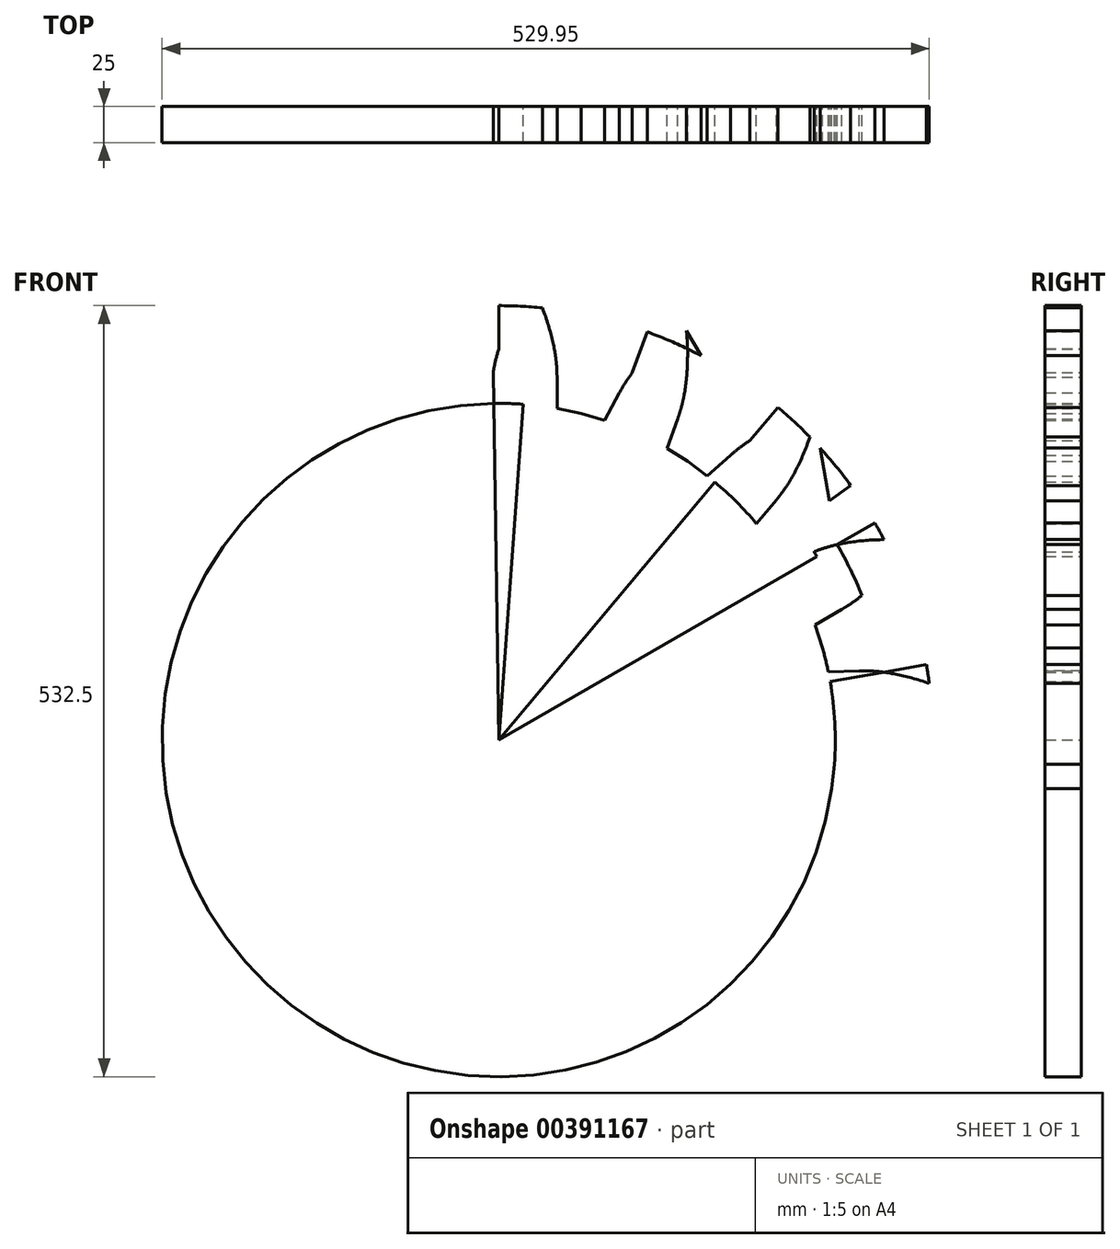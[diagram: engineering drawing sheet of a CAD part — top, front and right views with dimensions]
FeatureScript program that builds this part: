
annotation { "Feature Type Name" : "Feature", "Feature Type Description" : "" }
export const myFeature = defineFeature(function(context is Context, id is Id, definition is map)
    precondition{}
    {
        {
            var Q0;
            Q0=qCreatedBy(makeId("Front.planeOp"),FACE);
            var sketch = newSketch(context, id + "F0", { "sketchPlane" : qUnion([Q0])});
            skCircle(sketch, "E0", {"center": v(0, 0) * mm, "radius": 232.5 * mm});
            skCircle(sketch, "E1", {"center": v(0, 0) * mm, "radius": 253.72 * mm});
            skCircle(sketch, "E2", {"center": v(0, 0) * mm, "radius": 270 * mm});
            skCircle(sketch, "E3", {"center": v(0, 0) * mm, "radius": 300 * mm});
            skLineSegment(sketch, "E4", {"start": v(0, 0) * mm, "end": v(0, 396.68) * mm});
            skLineSegment(sketch, "E5", {"start": v(0, 0) * mm, "end": v(136.8, 375.88) * mm});
            skLineSegment(sketch, "E6", {"start": v(0, 0) * mm, "end": v(257.12, 306.42) * mm});
            skLineSegment(sketch, "E7", {"start": v(0, 0) * mm, "end": v(346.41, 200) * mm});
            skLineSegment(sketch, "E8", {"start": v(0, 270) * mm, "end": v(86.78, 238.41) * mm});
            skLineSegment(sketch, "E9", {"start": v(163.08, 194.36) * mm, "end": v(21.6, 313.07) * mm});
            skLineSegment(sketch, "E10", {"start": v(219.72, 126.86) * mm, "end": v(81.2, 366.78) * mm});
            skLineSegment(sketch, "E11", {"start": v(0, 0) * mm, "end": v(393.92, 69.46) * mm});
            skLineSegment(sketch, "E12", {"start": v(249.86, 44.06) * mm, "end": v(185.72, 407.83) * mm});
            skLineSegment(sketch, "E13", {"start": v(-5.96, 399.96) * mm, "end": v(0, 0) * mm});
            skFitSpline(sketch, "E14", {"points": [v(-3.78, 253.69) * mm, v(0, 270) * mm, v(21.6, 313.07) * mm, v(81.2, 366.78) * mm, v(185.72, 407.83) * mm], "startDerivative": vector(18.73, 108.77) * mm, "endDerivative": vector(322.57, 102.04) * mm});
            skLineSegment(sketch, "E15", {"start": v(21.69, 299.21) * mm, "end": v(0, 0) * mm});
            skFitSpline(sketch, "E16.MirrorCS", {"points": [v(40.33, 250.49) * mm, v(38.94, 267.18) * mm, v(23.77, 312.92) * mm, v(-27.46, 374.65) * mm, v(-124.96, 430.35) * mm], "startDerivative": vector(-2.85, 110.33) * mm, "endDerivative": vector(-304.48, 147.49) * mm});
            skFitSpline(sketch, "E17", {"points": [v(40.33, 250.49) * mm, v(40.33, 228.98) * mm], "startDerivative": vector(0, -16.2) * mm, "endDerivative": vector(0, -16.2) * mm});
            skFitSpline(sketch, "E18", {"points": [v(40.33, 228.98) * mm, v(56.82, 225.45) * mm], "startDerivative": vector(16.5, -3.53) * mm, "endDerivative": vector(16.5, -3.53) * mm});
            skArc(sketch, "E19.filletArc", {"start": v(40.33, 241.1) * mm, "mid": v(43.67, 231.67) * mm, "end": v(52.2, 226.44) * mm});
            skArc(sketch, "E20.MirrorCS", {"start": v(78.77, 231.42) * mm, "mid": v(71.36, 224.7) * mm, "end": v(61.37, 224.13) * mm});
            skFitSpline(sketch, "E21.MirrorCS", {"points": [v(73.02, 220.74) * mm, v(56.82, 225.45) * mm], "startDerivative": vector(-16.2, 4.71) * mm, "endDerivative": vector(-16.2, 4.71) * mm});
            skFitSpline(sketch, "E22.MirrorCS", {"points": [v(83.21, 239.68) * mm, v(92.35, 253.72) * mm, v(127.38, 286.8) * mm, v(201.75, 316.88) * mm, v(314, 319.71) * mm], "startDerivative": vector(54.8, 95.8) * mm, "endDerivative": vector(338.01, -14.44) * mm});
            skFitSpline(sketch, "E23.MirrorCS", {"points": [v(123.57, 221.59) * mm, v(127.97, 237.75) * mm, v(129.36, 285.91) * mm, v(102.33, 361.45) * mm, v(29.76, 447.13) * mm], "startDerivative": vector(35.06, 104.65) * mm, "endDerivative": vector(-235.67, 242.73) * mm});
            skFitSpline(sketch, "E24.MirrorCS", {"points": [v(83.21, 239.68) * mm, v(73.02, 220.74) * mm], "startDerivative": vector(-7.68, -14.27) * mm, "endDerivative": vector(-7.68, -14.27) * mm});
            skArc(sketch, "E25.MirrorCS", {"start": v(120.36, 212.77) * mm, "mid": v(120.27, 202.77) * mm, "end": v(126.5, 194.93) * mm});
            skFitSpline(sketch, "E26.MirrorCS", {"points": [v(116.21, 201.37) * mm, v(130.5, 192.42) * mm], "startDerivative": vector(14.3, -8.95) * mm, "endDerivative": vector(14.3, -8.95) * mm});
            skArc(sketch, "E27.MirrorCS", {"start": v(153.17, 190.52) * mm, "mid": v(143.9, 186.74) * mm, "end": v(134.32, 189.62) * mm});
            skFitSpline(sketch, "E28.MirrorCS", {"points": [v(144.1, 182.45) * mm, v(130.5, 192.42) * mm], "startDerivative": vector(-13.6, 9.97) * mm, "endDerivative": vector(-13.6, 9.97) * mm});
            skFitSpline(sketch, "E29.MirrorCS", {"points": [v(160.17, 196.77) * mm, v(173.55, 206.83) * mm, v(217.79, 225.94) * mm, v(297.97, 228.77) * mm, v(404.41, 193.03) * mm], "startDerivative": vector(84.26, 71.28) * mm, "endDerivative": vector(312.69, -129.18) * mm});
            skFitSpline(sketch, "E30.MirrorCS", {"points": [v(191.9, 165.96) * mm, v(201.57, 179.64) * mm, v(219.35, 224.43) * mm, v(219.79, 304.65) * mm, v(180.9, 409.99) * mm], "startDerivative": vector(68.74, 86.35) * mm, "endDerivative": vector(-138.44, 308.7) * mm});
            skArc(sketch, "E31.MirrorCS", {"start": v(185.87, 158.78) * mm, "mid": v(182.37, 149.4) * mm, "end": v(185.53, 139.91) * mm});
            skFitSpline(sketch, "E32.MirrorCS", {"points": [v(191.9, 165.96) * mm, v(178.08, 149.48) * mm], "startDerivative": vector(-10.41, -12.41) * mm, "endDerivative": vector(-10.41, -12.41) * mm});
            skFitSpline(sketch, "E33.MirrorCS", {"points": [v(217.8, 130.12) * mm, v(197.82, 122.16) * mm], "startDerivative": vector(-15.05, -6) * mm, "endDerivative": vector(-15.05, -6) * mm});
            skArc(sketch, "E34.MirrorCS", {"start": v(209.1, 126.65) * mm, "mid": v(199.1, 126.26) * mm, "end": v(191.08, 132.25) * mm});
            skFitSpline(sketch, "E35.MirrorCS", {"points": [v(217.8, 130.12) * mm, v(233.83, 135) * mm, v(281.93, 137.83) * mm, v(358.24, 113.06) * mm, v(446.05, 43.08) * mm], "startDerivative": vector(103.56, 38.16) * mm, "endDerivative": vector(249.65, -228.33) * mm});
            skFitSpline(sketch, "E36.MirrorCS", {"points": [v(237.1, 90.32) * mm, v(250.85, 99.87) * mm, v(282.88, 135.87) * mm, v(310.73, 211.1) * mm, v(310.2, 323.4) * mm], "startDerivative": vector(94.12, 57.63) * mm, "endDerivative": vector(-24.51, 337.43) * mm});
            skFitSpline(sketch, "E37.MirrorCS", {"points": [v(123.57, 221.59) * mm, v(116.21, 201.37) * mm], "startDerivative": vector(-5.54, -15.22) * mm, "endDerivative": vector(-5.54, -15.22) * mm});
            skFitSpline(sketch, "E38.MirrorCS", {"points": [v(160.17, 196.77) * mm, v(144.1, 182.45) * mm], "startDerivative": vector(-12.1, -10.78) * mm, "endDerivative": vector(-12.1, -10.78) * mm});
            skLineSegment(sketch, "E39", {"start": v(0, 0) * mm, "end": v(327.9, 236.96) * mm});
            skFitSpline(sketch, "E40.MirrorCS", {"points": [v(217.8, 130.12) * mm, v(197.82, 122.16) * mm], "startDerivative": vector(-15.05, -6) * mm, "endDerivative": vector(-15.05, -6) * mm});
            skArc(sketch, "E41.MirrorCS", {"start": v(228.97, 85.63) * mm, "mid": v(222.47, 78.02) * mm, "end": v(222.2, 68.02) * mm});
            skFitSpline(sketch, "E42.MirrorCS", {"points": [v(237.1, 90.32) * mm, v(218.46, 79.56) * mm], "startDerivative": vector(-14.03, -8.1) * mm, "endDerivative": vector(-14.03, -8.1) * mm});
            skFitSpline(sketch, "E43.MirrorCS", {"points": [v(218.46, 79.56) * mm, v(223.66, 63.52) * mm], "startDerivative": vector(5.2, -16.05) * mm, "endDerivative": vector(5.2, -16.05) * mm});
            skArc(sketch, "E44.MirrorCS", {"start": v(239.8, 47.5) * mm, "mid": v(230.27, 50.55) * mm, "end": v(224.78, 58.92) * mm});
            skFitSpline(sketch, "E45.MirrorCS", {"points": [v(249.18, 47.78) * mm, v(227.67, 47.14) * mm], "startDerivative": vector(-16.2, -0.48) * mm, "endDerivative": vector(-16.2, -0.48) * mm});
            skFitSpline(sketch, "E46.MirrorCS", {"points": [v(249.18, 47.78) * mm, v(265.9, 46.89) * mm, v(312.07, 33.09) * mm, v(375.3, -16.28) * mm, v(433.88, -112.08) * mm], "startDerivative": vector(110.36, 0.44) * mm, "endDerivative": vector(156.5, -299.95) * mm});
            skFitSpline(sketch, "E47.MirrorCS", {"points": [v(253.69, 3.78) * mm, v(269.88, 8.05) * mm, v(312.3, 30.93) * mm, v(364.2, 92.1) * mm, v(402.1, 197.8) * mm], "startDerivative": vector(108.16, 21.96) * mm, "endDerivative": vector(92.38, 325.46) * mm});
            skFitSpline(sketch, "E48.MirrorCS", {"points": [v(217.8, 130.12) * mm, v(233.83, 135) * mm, v(281.93, 137.83) * mm, v(358.24, 113.06) * mm, v(446.05, 43.08) * mm], "startDerivative": vector(103.56, 38.16) * mm, "endDerivative": vector(249.65, -228.33) * mm});
            skFitSpline(sketch, "E49.MirrorCS", {"points": [v(237.1, 90.32) * mm, v(250.85, 99.87) * mm, v(282.88, 135.87) * mm, v(310.73, 211.1) * mm, v(310.2, 323.4) * mm], "startDerivative": vector(94.12, 57.63) * mm, "endDerivative": vector(-24.51, 337.43) * mm});
            skFitSpline(sketch, "E50.MirrorCS", {"points": [v(250.49, -40.33) * mm, v(265.9, -46.89) * mm, v(304.57, -75.64) * mm, v(347.1, -143.66) * mm, v(369.38, -253.71) * mm], "startDerivative": vector(103.86, -37.33) * mm, "endDerivative": vector(44.47, -335.38) * mm});
            skFitSpline(sketch, "E51.MirrorCS", {"points": [v(239.68, -83.21) * mm, v(256.36, -84.74) * mm, v(304.03, -77.75) * mm, v(373.73, -38.01) * mm, v(445.5, 48.33) * mm], "startDerivative": vector(109.15, -16.36) * mm, "endDerivative": vector(198.12, 274.24) * mm});
            skArc(sketch, "E52.MirrorCS", {"start": v(241.58, -37.38) * mm, "mid": v(233.67, -31.25) * mm, "end": v(231.38, -21.52) * mm});
            skFitSpline(sketch, "E53.MirrorCS", {"points": [v(250.49, -40.33) * mm, v(230.06, -33.58) * mm], "startDerivative": vector(-15.38, 5.08) * mm, "endDerivative": vector(-15.38, 5.08) * mm});
            skFitSpline(sketch, "E54.MirrorCS", {"points": [v(230.06, -33.58) * mm, v(231.9, -16.8) * mm], "startDerivative": vector(1.83, 16.77) * mm, "endDerivative": vector(1.83, 16.77) * mm});
            skSolve(sketch);
        }
        {
            var Q0;
            {var subQ5=sQuery(id+"F0.wireOp",EDGE,"E54.MirrorCS");Q0=makeQuery(id+"F0.imprint","IMPRINT",FACE,{"disambiguationData":[TD([[makeQuery(id+"F0.imprint","IMPRINT",EDGE,{"derivedFrom":subQ5}),1.0]])]});}
            var Q1;
            {var subQ1=sQuery(id+"F0.wireOp",EDGE,"E4");var subQ3=sQuery(id+"F0.wireOp",EDGE,"E0");var subQ4=makeQuery(id+"F0.imprint","INTERSECT",VERTEX,{"derivedFrom":[subQ1,subQ3]});Q1=makeQuery(id+"F0.imprint","IMPRINT",FACE,{"disambiguationData":[TD([[makeQuery(id+"F0.imprint","IMPRINT",EDGE,{"disambiguationData":[TD([[subQ4,-1.0]])],"derivedFrom":subQ3}),-1.0]])]});}
            var Q2;
            {var subQ1=sQuery(id+"F0.wireOp",EDGE,"E4");var subQ3=sQuery(id+"F0.wireOp",EDGE,"E0");var subQ4=makeQuery(id+"F0.imprint","INTERSECT",VERTEX,{"derivedFrom":[subQ1,subQ3]});Q2=makeQuery(id+"F0.imprint","IMPRINT",FACE,{"disambiguationData":[TD([[makeQuery(id+"F0.imprint","IMPRINT",EDGE,{"disambiguationData":[TD([[subQ4,1.0]])],"derivedFrom":subQ3}),-1.0]])]});}
            var Q3;
            {var subQ0=sQuery(id+"F0.wireOp",EDGE,"E17");Q3=makeQuery(id+"F0.imprint","IMPRINT",FACE,{"disambiguationData":[TD([[makeQuery(id+"F0.imprint","IMPRINT",EDGE,{"derivedFrom":subQ0}),-1.0]])]});}
            var Q4;
            {var subQ0=sQuery(id+"F0.wireOp",EDGE,"E15");var subQ1=sQuery(id+"F0.wireOp",EDGE,"E1");var subQ2=makeQuery(id+"F0.imprint","INTERSECT",VERTEX,{"derivedFrom":[subQ1,subQ0]});Q4=makeQuery(id+"F0.imprint","IMPRINT",FACE,{"disambiguationData":[TD([[makeQuery(id+"F0.imprint","IMPRINT",EDGE,{"disambiguationData":[TD([[subQ2,-1.0]])],"derivedFrom":subQ1}),1.0]])]});}
            var Q5;
            {var subQ0=sQuery(id+"F0.wireOp",EDGE,"E16.MirrorCS");var subQ1=sQuery(id+"F0.wireOp",EDGE,"E2");var subQ2=makeQuery(id+"F0.imprint","INTERSECT",VERTEX,{"derivedFrom":[subQ1,subQ0]});Q5=makeQuery(id+"F0.imprint","IMPRINT",FACE,{"disambiguationData":[TD([[makeQuery(id+"F0.imprint","IMPRINT",EDGE,{"disambiguationData":[TD([[subQ2,-1.0]])],"derivedFrom":subQ1}),1.0]])]});}
            var Q6;
            {var subQ3=sQuery(id+"F0.wireOp",EDGE,"E15");var subQ5=sQuery(id+"F0.wireOp",EDGE,"E8");var subQ6=makeQuery(id+"F0.imprint","INTERSECT",VERTEX,{"derivedFrom":[subQ5,subQ3]});Q6=makeQuery(id+"F0.imprint","IMPRINT",FACE,{"disambiguationData":[TD([[makeQuery(id+"F0.imprint","IMPRINT",EDGE,{"disambiguationData":[TD([[subQ6,-1.0]])],"derivedFrom":subQ5}),-1.0]])]});}
            var Q7;
            {var subQ0=sQuery(id+"F0.wireOp",EDGE,"E15");var subQ1=sQuery(id+"F0.wireOp",EDGE,"E1");var subQ2=makeQuery(id+"F0.imprint","INTERSECT",VERTEX,{"derivedFrom":[subQ1,subQ0]});Q7=makeQuery(id+"F0.imprint","IMPRINT",FACE,{"disambiguationData":[TD([[makeQuery(id+"F0.imprint","IMPRINT",EDGE,{"disambiguationData":[TD([[subQ2,-1.0]])],"derivedFrom":subQ1}),-1.0]])]});}
            var Q8;
            {var subQ1=sQuery(id+"F0.wireOp",EDGE,"E1");var subQ3=sQuery(id+"F0.wireOp",EDGE,"E4");var subQ4=makeQuery(id+"F0.imprint","INTERSECT",VERTEX,{"derivedFrom":[subQ1,subQ3]});Q8=makeQuery(id+"F0.imprint","IMPRINT",FACE,{"disambiguationData":[TD([[makeQuery(id+"F0.imprint","IMPRINT",EDGE,{"disambiguationData":[TD([[subQ4,1.0]])],"derivedFrom":subQ3}),1.0]])]});}
            var Q9;
            {var subQ1=sQuery(id+"F0.wireOp",EDGE,"E1");var subQ3=sQuery(id+"F0.wireOp",EDGE,"E4");var subQ4=makeQuery(id+"F0.imprint","INTERSECT",VERTEX,{"derivedFrom":[subQ1,subQ3]});Q9=makeQuery(id+"F0.imprint","IMPRINT",FACE,{"disambiguationData":[TD([[makeQuery(id+"F0.imprint","IMPRINT",EDGE,{"disambiguationData":[TD([[subQ4,-1.0]])],"derivedFrom":subQ1}),-1.0]])]});}
            var Q10;
            {var subQ3=sQuery(id+"F0.wireOp",EDGE,"E15");var subQ5=sQuery(id+"F0.wireOp",EDGE,"E3");var subQ7=makeQuery(id+"F0.imprint","INTERSECT",VERTEX,{"derivedFrom":[subQ5,subQ3]});Q10=makeQuery(id+"F0.imprint","IMPRINT",FACE,{"disambiguationData":[TD([[makeQuery(id+"F0.imprint","IMPRINT",EDGE,{"disambiguationData":[TD([[subQ7,-1.0]])],"derivedFrom":subQ5}),1.0]])]});}
            var Q11;
            {var subQ0=sQuery(id+"F0.wireOp",EDGE,"E16.MirrorCS");var subQ1=sQuery(id+"F0.wireOp",EDGE,"E2");var subQ2=makeQuery(id+"F0.imprint","INTERSECT",VERTEX,{"derivedFrom":[subQ1,subQ0]});Q11=makeQuery(id+"F0.imprint","IMPRINT",FACE,{"disambiguationData":[TD([[makeQuery(id+"F0.imprint","IMPRINT",EDGE,{"disambiguationData":[TD([[subQ2,-1.0]])],"derivedFrom":subQ1}),-1.0]])]});}
            var Q12;
            {var subQ1=sQuery(id+"F0.wireOp",EDGE,"E2");var subQ3=sQuery(id+"F0.wireOp",EDGE,"E15");var subQ4=makeQuery(id+"F0.imprint","INTERSECT",VERTEX,{"derivedFrom":[subQ1,subQ3]});Q12=makeQuery(id+"F0.imprint","IMPRINT",FACE,{"disambiguationData":[TD([[makeQuery(id+"F0.imprint","IMPRINT",EDGE,{"disambiguationData":[TD([[subQ4,-1.0]])],"derivedFrom":subQ3}),-1.0]])]});}
            var Q13;
            {var subQ1=sQuery(id+"F0.wireOp",EDGE,"E18");Q13=makeQuery(id+"F0.imprint","IMPRINT",FACE,{"disambiguationData":[TD([[makeQuery(id+"F0.imprint","IMPRINT",EDGE,{"derivedFrom":subQ1}),-1.0]])]});}
            var Q14;
            {var subQ0=sQuery(id+"F0.wireOp",EDGE,"E26.MirrorCS");Q14=makeQuery(id+"F0.imprint","IMPRINT",FACE,{"disambiguationData":[TD([[makeQuery(id+"F0.imprint","IMPRINT",EDGE,{"derivedFrom":subQ0}),-1.0]])]});}
            var Q15;
            {var subQ1=sQuery(id+"F0.wireOp",EDGE,"E24.MirrorCS");Q15=makeQuery(id+"F0.imprint","IMPRINT",FACE,{"disambiguationData":[TD([[makeQuery(id+"F0.imprint","IMPRINT",EDGE,{"derivedFrom":subQ1}),1.0]])]});}
            var Q16;
            {var subQ5=sQuery(id+"F0.wireOp",EDGE,"E37.MirrorCS");Q16=makeQuery(id+"F0.imprint","IMPRINT",FACE,{"disambiguationData":[TD([[makeQuery(id+"F0.imprint","IMPRINT",EDGE,{"derivedFrom":subQ5}),-1.0]])]});}
            var Q17;
            {var subQ0=sQuery(id+"F0.wireOp",EDGE,"E5");var subQ5=sQuery(id+"F0.wireOp",EDGE,"E9");var subQ7=makeQuery(id+"F0.imprint","INTERSECT",VERTEX,{"derivedFrom":[subQ0,subQ5]});Q17=makeQuery(id+"F0.imprint","IMPRINT",FACE,{"disambiguationData":[TD([[makeQuery(id+"F0.imprint","IMPRINT",EDGE,{"disambiguationData":[TD([[subQ7,1.0]])],"derivedFrom":subQ5}),1.0]])]});}
            var Q18;
            {var subQ0=sQuery(id+"F0.wireOp",EDGE,"E23.MirrorCS");var subQ5=sQuery(id+"F0.wireOp",EDGE,"E3");var subQ6=makeQuery(id+"F0.imprint","INTERSECT",VERTEX,{"derivedFrom":[subQ5,subQ0]});Q18=makeQuery(id+"F0.imprint","IMPRINT",FACE,{"disambiguationData":[TD([[makeQuery(id+"F0.imprint","IMPRINT",EDGE,{"disambiguationData":[TD([[subQ6,-1.0]])],"derivedFrom":subQ5}),1.0]])]});}
            var Q19;
            {var subQ3=sQuery(id+"F0.wireOp",EDGE,"E5");var subQ5=sQuery(id+"F0.wireOp",EDGE,"E9");var subQ6=makeQuery(id+"F0.imprint","INTERSECT",VERTEX,{"derivedFrom":[subQ3,subQ5]});Q19=makeQuery(id+"F0.imprint","IMPRINT",FACE,{"disambiguationData":[TD([[makeQuery(id+"F0.imprint","IMPRINT",EDGE,{"disambiguationData":[TD([[subQ6,1.0]])],"derivedFrom":subQ5}),-1.0]])]});}
            var Q20;
            {var subQ1=sQuery(id+"F0.wireOp",EDGE,"E5");var subQ3=sQuery(id+"F0.wireOp",EDGE,"E9");var subQ4=makeQuery(id+"F0.imprint","INTERSECT",VERTEX,{"derivedFrom":[subQ1,subQ3]});Q20=makeQuery(id+"F0.imprint","IMPRINT",FACE,{"disambiguationData":[TD([[makeQuery(id+"F0.imprint","IMPRINT",EDGE,{"disambiguationData":[TD([[subQ4,-1.0]])],"derivedFrom":subQ3}),1.0]])]});}
            var Q21;
            {var subQ0=sQuery(id+"F0.wireOp",EDGE,"E38.MirrorCS");Q21=makeQuery(id+"F0.imprint","IMPRINT",FACE,{"disambiguationData":[TD([[makeQuery(id+"F0.imprint","IMPRINT",EDGE,{"derivedFrom":subQ0}),1.0]])]});}
            var Q22;
            {var subQ0=sQuery(id+"F0.wireOp",EDGE,"E32.MirrorCS");Q22=makeQuery(id+"F0.imprint","IMPRINT",FACE,{"disambiguationData":[TD([[makeQuery(id+"F0.imprint","IMPRINT",EDGE,{"derivedFrom":subQ0}),-1.0]])]});}
            var Q23;
            {var subQ3=sQuery(id+"F0.wireOp",EDGE,"E0");var subQ6=makeQuery(id+"F0.imprint","INTERSECT",VERTEX,{"derivedFrom":[sQuery(id+"F0.wireOp",EDGE,"E31.MirrorCS"),subQ3]});Q23=makeQuery(id+"F0.imprint","IMPRINT",FACE,{"disambiguationData":[TD([[makeQuery(id+"F0.imprint","IMPRINT",EDGE,{"disambiguationData":[TD([[subQ6,1.0]])],"derivedFrom":subQ3}),-1.0]])]});}
            var Q24;
            {var subQ0=sQuery(id+"F0.wireOp",EDGE,"E6");var subQ5=sQuery(id+"F0.wireOp",EDGE,"E10");var subQ6=makeQuery(id+"F0.imprint","INTERSECT",VERTEX,{"derivedFrom":[subQ0,subQ5]});Q24=makeQuery(id+"F0.imprint","IMPRINT",FACE,{"disambiguationData":[TD([[makeQuery(id+"F0.imprint","IMPRINT",EDGE,{"disambiguationData":[TD([[subQ6,1.0]])],"derivedFrom":subQ5}),1.0]])]});}
            var Q25;
            {var subQ1=sQuery(id+"F0.wireOp",EDGE,"E6");var subQ3=sQuery(id+"F0.wireOp",EDGE,"E10");var subQ4=makeQuery(id+"F0.imprint","INTERSECT",VERTEX,{"derivedFrom":[subQ1,subQ3]});Q25=makeQuery(id+"F0.imprint","IMPRINT",FACE,{"disambiguationData":[TD([[makeQuery(id+"F0.imprint","IMPRINT",EDGE,{"disambiguationData":[TD([[subQ4,-1.0]])],"derivedFrom":subQ3}),1.0]])]});}
            var Q26;
            {var subQ3=sQuery(id+"F0.wireOp",EDGE,"E6");var subQ5=sQuery(id+"F0.wireOp",EDGE,"E10");var subQ6=makeQuery(id+"F0.imprint","INTERSECT",VERTEX,{"derivedFrom":[subQ3,subQ5]});Q26=makeQuery(id+"F0.imprint","IMPRINT",FACE,{"disambiguationData":[TD([[makeQuery(id+"F0.imprint","IMPRINT",EDGE,{"disambiguationData":[TD([[subQ6,1.0]])],"derivedFrom":subQ5}),-1.0]])]});}
            var Q27;
            {var subQ0=sQuery(id+"F0.wireOp",EDGE,"E30.MirrorCS");var subQ5=sQuery(id+"F0.wireOp",EDGE,"E3");var subQ6=makeQuery(id+"F0.imprint","INTERSECT",VERTEX,{"derivedFrom":[subQ5,subQ0]});Q27=makeQuery(id+"F0.imprint","IMPRINT",FACE,{"disambiguationData":[TD([[makeQuery(id+"F0.imprint","IMPRINT",EDGE,{"disambiguationData":[TD([[subQ6,-1.0]])],"derivedFrom":subQ5}),1.0]])]});}
            var Q28;
            {var subQ0=sQuery(id+"F0.wireOp",EDGE,"E40.MirrorCS");Q28=makeQuery(id+"F0.imprint","IMPRINT",FACE,{"disambiguationData":[TD([[makeQuery(id+"F0.imprint","IMPRINT",EDGE,{"derivedFrom":subQ0}),1.0]])]});}
            var Q29;
            {var subQ3=sQuery(id+"F0.wireOp",EDGE,"E0");var subQ5=makeQuery(id+"F0.imprint","INTERSECT",VERTEX,{"derivedFrom":[sQuery(id+"F0.wireOp",EDGE,"E34.MirrorCS"),subQ3]});Q29=makeQuery(id+"F0.imprint","IMPRINT",FACE,{"disambiguationData":[TD([[makeQuery(id+"F0.imprint","IMPRINT",EDGE,{"disambiguationData":[TD([[subQ5,1.0]])],"derivedFrom":subQ3}),-1.0]])]});}
            var Q30;
            {var subQ0=sQuery(id+"F0.wireOp",EDGE,"E42.MirrorCS");Q30=makeQuery(id+"F0.imprint","IMPRINT",FACE,{"disambiguationData":[TD([[makeQuery(id+"F0.imprint","IMPRINT",EDGE,{"derivedFrom":subQ0}),-1.0]])]});}
            var Q31;
            {var subQ1=sQuery(id+"F0.wireOp",EDGE,"E7");var subQ3=sQuery(id+"F0.wireOp",EDGE,"E12");var subQ4=makeQuery(id+"F0.imprint","INTERSECT",VERTEX,{"derivedFrom":[subQ1,subQ3]});Q31=makeQuery(id+"F0.imprint","IMPRINT",FACE,{"disambiguationData":[TD([[makeQuery(id+"F0.imprint","IMPRINT",EDGE,{"disambiguationData":[TD([[subQ4,-1.0]])],"derivedFrom":subQ3}),1.0]])]});}
            var Q32;
            {var subQ0=sQuery(id+"F0.wireOp",EDGE,"E7");var subQ5=sQuery(id+"F0.wireOp",EDGE,"E12");var subQ6=makeQuery(id+"F0.imprint","INTERSECT",VERTEX,{"derivedFrom":[subQ0,subQ5]});Q32=makeQuery(id+"F0.imprint","IMPRINT",FACE,{"disambiguationData":[TD([[makeQuery(id+"F0.imprint","IMPRINT",EDGE,{"disambiguationData":[TD([[subQ6,1.0]])],"derivedFrom":subQ5}),1.0]])]});}
            var Q33;
            {var subQ3=sQuery(id+"F0.wireOp",EDGE,"E7");var subQ5=sQuery(id+"F0.wireOp",EDGE,"E12");var subQ7=makeQuery(id+"F0.imprint","INTERSECT",VERTEX,{"derivedFrom":[subQ3,subQ5]});Q33=makeQuery(id+"F0.imprint","IMPRINT",FACE,{"disambiguationData":[TD([[makeQuery(id+"F0.imprint","IMPRINT",EDGE,{"disambiguationData":[TD([[subQ7,1.0]])],"derivedFrom":subQ5}),-1.0]])]});}
            var Q34;
            {var subQ0=sQuery(id+"F0.wireOp",EDGE,"E43.MirrorCS");Q34=makeQuery(id+"F0.imprint","IMPRINT",FACE,{"disambiguationData":[TD([[makeQuery(id+"F0.imprint","IMPRINT",EDGE,{"derivedFrom":subQ0}),-1.0]])]});}
            var Q35;
            {var subQ0=sQuery(id+"F0.wireOp",EDGE,"E49.MirrorCS");var subQ5=sQuery(id+"F0.wireOp",EDGE,"E3");var subQ7=makeQuery(id+"F0.imprint","INTERSECT",VERTEX,{"derivedFrom":[subQ5,subQ0]});Q35=makeQuery(id+"F0.imprint","IMPRINT",FACE,{"disambiguationData":[TD([[makeQuery(id+"F0.imprint","IMPRINT",EDGE,{"disambiguationData":[TD([[subQ7,-1.0]])],"derivedFrom":subQ5}),1.0]])]});}
            var Q36;
            {var subQ5=sQuery(id+"F0.wireOp",EDGE,"E45.MirrorCS");Q36=makeQuery(id+"F0.imprint","IMPRINT",FACE,{"disambiguationData":[TD([[makeQuery(id+"F0.imprint","IMPRINT",EDGE,{"derivedFrom":subQ5}),1.0]])]});}
            var Q37;
            {var subQ0=sQuery(id+"F0.wireOp",EDGE,"E12");var subQ3=sQuery(id+"F0.wireOp",EDGE,"E46.MirrorCS");var subQ5=makeQuery(id+"F0.imprint","INTERSECT",VERTEX,{"derivedFrom":[subQ0,subQ3]});Q37=makeQuery(id+"F0.imprint","IMPRINT",FACE,{"disambiguationData":[TD([[makeQuery(id+"F0.imprint","IMPRINT",EDGE,{"disambiguationData":[TD([[subQ5,1.0]])],"derivedFrom":subQ0}),-1.0]])]});}
            var Q38;
            {var subQ0=sQuery(id+"F0.wireOp",EDGE,"E9");var subQ3=sQuery(id+"F0.wireOp",EDGE,"E29.MirrorCS");var subQ5=makeQuery(id+"F0.imprint","INTERSECT",VERTEX,{"derivedFrom":[subQ0,subQ3]});Q38=makeQuery(id+"F0.imprint","IMPRINT",FACE,{"disambiguationData":[TD([[makeQuery(id+"F0.imprint","IMPRINT",EDGE,{"disambiguationData":[TD([[subQ5,1.0]])],"derivedFrom":subQ0}),1.0]])]});}
            var Q39;
            {var subQ0=sQuery(id+"F0.wireOp",EDGE,"E10");var subQ3=sQuery(id+"F0.wireOp",EDGE,"E48.MirrorCS");var subQ5=makeQuery(id+"F0.imprint","INTERSECT",VERTEX,{"derivedFrom":[subQ0,subQ3]});Q39=makeQuery(id+"F0.imprint","IMPRINT",FACE,{"disambiguationData":[TD([[makeQuery(id+"F0.imprint","IMPRINT",EDGE,{"disambiguationData":[TD([[subQ5,1.0]])],"derivedFrom":subQ0}),1.0]])]});}
            var Q40;
            {var subQ0=sQuery(id+"F0.wireOp",EDGE,"E12");var subQ3=sQuery(id+"F0.wireOp",EDGE,"E46.MirrorCS");var subQ5=makeQuery(id+"F0.imprint","INTERSECT",VERTEX,{"derivedFrom":[subQ0,subQ3]});Q40=makeQuery(id+"F0.imprint","IMPRINT",FACE,{"disambiguationData":[TD([[makeQuery(id+"F0.imprint","IMPRINT",EDGE,{"disambiguationData":[TD([[subQ5,1.0]])],"derivedFrom":subQ0}),1.0]])]});}
            var Q41;
            {var subQ0=sQuery(id+"F0.wireOp",EDGE,"E8");var subQ3=sQuery(id+"F0.wireOp",EDGE,"E22.MirrorCS");var subQ5=makeQuery(id+"F0.imprint","INTERSECT",VERTEX,{"derivedFrom":[subQ0,subQ3]});Q41=makeQuery(id+"F0.imprint","IMPRINT",FACE,{"disambiguationData":[TD([[makeQuery(id+"F0.imprint","IMPRINT",EDGE,{"disambiguationData":[TD([[subQ5,-1.0]])],"derivedFrom":subQ0}),-1.0]])]});}
            extrude(context, id + "F1", {"entities" : qUnion([Q0, Q1, Q2, Q3, Q4, Q5, Q6, Q7, Q8, Q9, Q10, Q11, Q12, Q13, Q14, Q15, Q16, Q17, Q18, Q19, Q20, Q21, Q22, Q23, Q24, Q25, Q26, Q27, Q28, Q29, Q30, Q31, Q32, Q33, Q34, Q35, Q36, Q37, Q38, Q39, Q40, Q41]), "depth" : 25 * mm});
        }
    });
